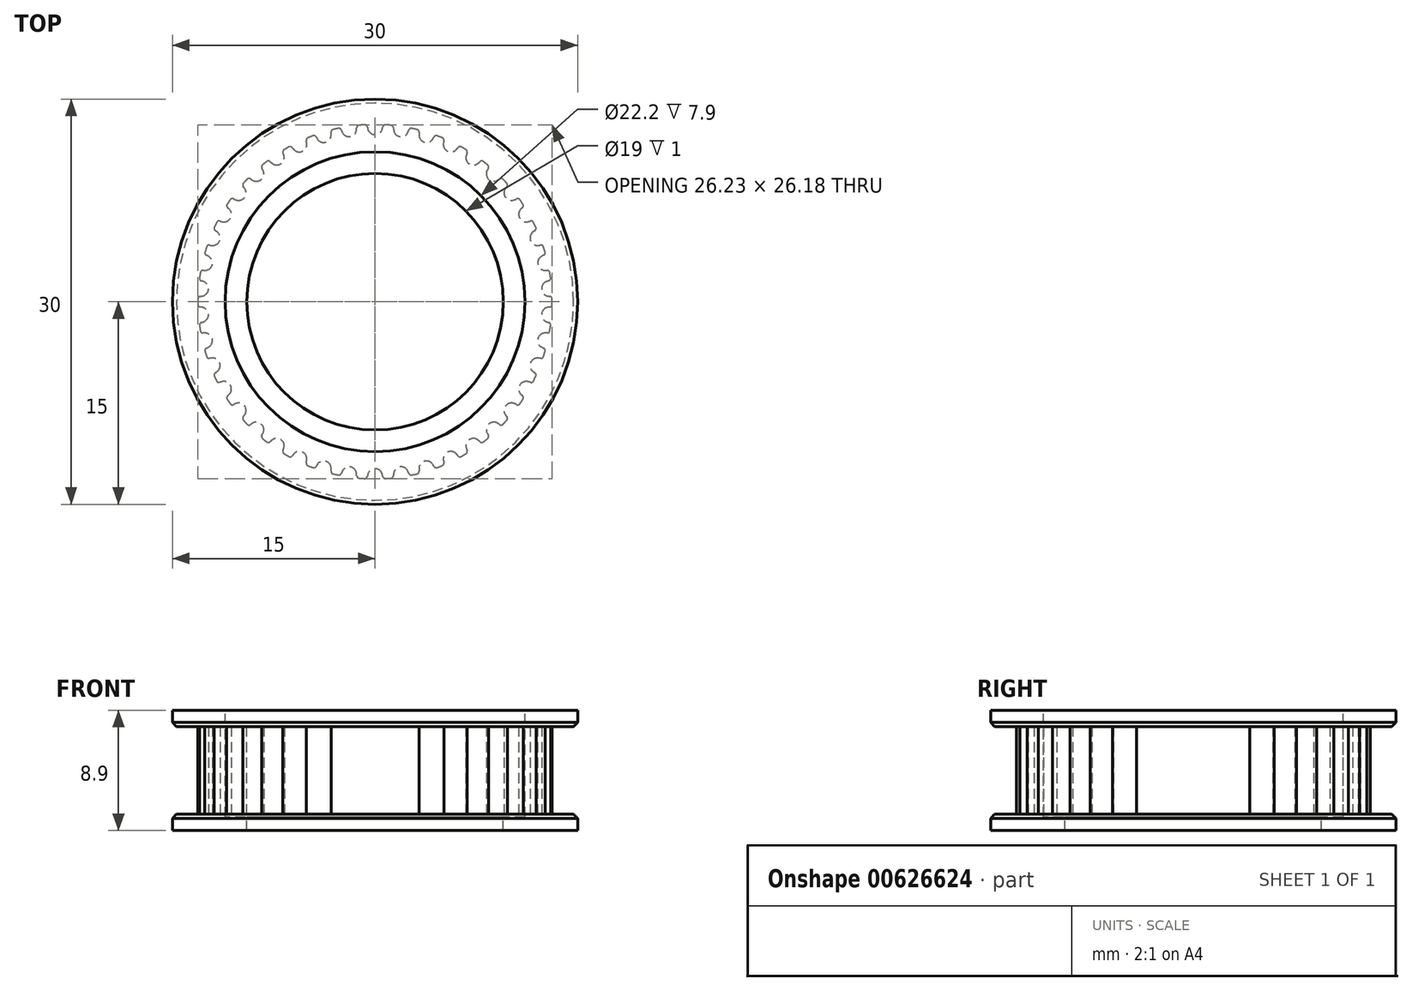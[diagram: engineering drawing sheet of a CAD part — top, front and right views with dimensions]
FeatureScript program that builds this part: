
annotation { "Feature Type Name" : "Feature", "Feature Type Description" : "" }
export const myFeature = defineFeature(function(context is Context, id is Id, definition is map)
    precondition{}
    {
        {
            assignVariable(context, id + "F0", {"name" : "teeth", "anyValue" : 42});
        }
        {
            assignVariable(context, id + "F1", {"name" : "belt_width", "anyValue" : 6.5});
        }
        {
            var Q0;
            Q0=qCreatedBy(makeId("Top.planeOp"),FACE);
            var sketch = newSketch(context, id + "F2", { "sketchPlane" : qUnion([Q0])});
            skLineSegment(sketch, "E0", {"start": v(0, 0) * mm, "end": v(0, 12.37) * mm, "construction": true});
            skCircle(sketch, "E1", {"center": v(0, 0) * mm, "radius": 13.12 * mm});
            skPoint(sketch, "E2.MirrorCS.end.orphan", {"position": v(0.98, 13.08) * mm});
            skLineSegment(sketch, "E3", {"start": v(0.98, 13.08) * mm, "end": v(1, 13.33) * mm, "construction": true});
            skLineSegment(sketch, "E4", {"start": v(-0.98, 13.08) * mm, "end": v(-1, 13.33) * mm, "construction": true});
            skArc(sketch, "E5", {"start": v(0, 12.37) * mm, "mid": v(0.34, 12.48) * mm, "end": v(0.54, 12.77) * mm});
            skArc(sketch, "E6", {"start": v(0.54, 12.77) * mm, "mid": v(0.56, 12.87) * mm, "end": v(0.58, 12.97) * mm, "construction": true});
            skLineSegment(sketch, "E7", {"start": v(0, 12.37) * mm, "end": v(0, 13.12) * mm, "construction": true});
            skLineSegment(sketch, "E8", {"start": v(0, 13.12) * mm, "end": v(0, 13.37) * mm, "construction": true});
            skArc(sketch, "E9", {"start": v(0.58, 12.97) * mm, "mid": v(0.64, 13.06) * mm, "end": v(0.74, 13.1) * mm, "construction": true});
            skArc(sketch, "E10", {"start": v(1, 13.33) * mm, "mid": v(0, 13.37) * mm, "end": v(-1, 13.33) * mm, "construction": true});
            skLineSegment(sketch, "E11", {"start": v(0.98, 13.08) * mm, "end": v(0.92, 12.33) * mm});
            skLineSegment(sketch, "E12", {"start": v(0.92, 12.33) * mm, "end": v(0, 0) * mm});
            skLineSegment(sketch, "E13", {"start": v(0, 0) * mm, "end": v(-0.92, 12.33) * mm});
            skLineSegment(sketch, "E14", {"start": v(-0.92, 12.33) * mm, "end": v(-0.98, 13.08) * mm});
            skArc(sketch, "E15", {"start": v(0.77, 13.1) * mm, "mid": v(0.65, 13.06) * mm, "end": v(0.58, 12.95) * mm});
            skArc(sketch, "E16", {"start": v(0.54, 12.77) * mm, "mid": v(0.56, 12.86) * mm, "end": v(0.58, 12.95) * mm});
            skArc(sketch, "E17.MirrorCS", {"start": v(0, 12.37) * mm, "mid": v(-0.34, 12.48) * mm, "end": v(-0.54, 12.77) * mm});
            skArc(sketch, "E18.MirrorCS", {"start": v(-0.54, 12.77) * mm, "mid": v(-0.56, 12.86) * mm, "end": v(-0.58, 12.95) * mm});
            skArc(sketch, "E19.MirrorCS", {"start": v(-0.77, 13.1) * mm, "mid": v(-0.65, 13.06) * mm, "end": v(-0.58, 12.95) * mm});
            skArc(sketch, "E20", {"start": v(0, 13.12) * mm, "mid": v(-0.2, 13.11) * mm, "end": v(-0.4, 13.1) * mm});
            skArc(sketch, "E21", {"start": v(0.92, 12.33) * mm, "mid": v(0, 12.37) * mm, "end": v(-0.92, 12.33) * mm, "construction": true});
            skLineSegment(sketch, "E22", {"start": v(1, 13.33) * mm, "end": v(1.03, 13.7) * mm, "construction": true});
            skLineSegment(sketch, "E23", {"start": v(-1, 13.33) * mm, "end": v(-1.03, 13.7) * mm, "construction": true});
            skArc(sketch, "E24", {"start": v(-1.03, 13.7) * mm, "mid": v(0, 13.75) * mm, "end": v(1.03, 13.7) * mm, "construction": true});
            skSolve(sketch);
        }
        {
            var Q0;
            Q0=makeQuery(id+"F2.imprint","IMPRINT",FACE,{"disambiguationData":[TD([[makeQuery(id+"F2.imprint","IMPRINT",EDGE,{"derivedFrom":sQuery(id+"F2.wireOp",EDGE,"E5")}),-1.0]])]});
            var Q1;
            {var subQ1=sQuery(id+"F2.wireOp",EDGE,"E14");Q1=makeQuery(id+"F2.imprint","IMPRINT",FACE,{"disambiguationData":[TD([[makeQuery(id+"F2.imprint","IMPRINT",EDGE,{"derivedFrom":subQ1}),-1.0]])]});}
            var Q2;
            {var subQ0=sQuery(id+"F2.wireOp",EDGE,"E12");Q2=makeQuery(id+"F2.imprint","IMPRINT",FACE,{"disambiguationData":[TD([[makeQuery(id+"F2.imprint","IMPRINT",EDGE,{"derivedFrom":subQ0}),-1.0]])]});}
            extrude(context, id + "F3", {"entities" : qUnion([Q0, Q1, Q2]), "depth" : (getVariable(context, 'belt_width')) * mm, "symmetric" : true});
        }
        {
            var Q0;
            Q0=makeQuery(id+"F3.opExtrude","SWEPT_BODY",BODY,{"disambiguationData":[OSD([sQuery(id+"F2.wireOp",EDGE,"E1"),sQuery(id+"F2.wireOp",EDGE,"E5"),sQuery(id+"F2.wireOp",EDGE,"E11"),sQuery(id+"F2.wireOp",EDGE,"E12"),sQuery(id+"F2.wireOp",EDGE,"E13"),sQuery(id+"F2.wireOp",EDGE,"E14"),sQuery(id+"F2.wireOp",EDGE,"E15"),sQuery(id+"F2.wireOp",EDGE,"E16"),sQuery(id+"F2.wireOp",EDGE,"E17.MirrorCS"),sQuery(id+"F2.wireOp",EDGE,"E18.MirrorCS"),sQuery(id+"F2.wireOp",EDGE,"E19.MirrorCS")])]});
            var Q1;
            Q1=makeQuery(id+"F3.opExtrude","SWEPT_EDGE",EDGE,{"disambiguationData":[OSD([sQuery(id+"F2.wireOp",EDGE,"E12"),sQuery(id+"F2.wireOp",EDGE,"E13")])]});
            circularPattern(context, id + "F4", {"operationType" : NewBodyOperationType.ADD, "entities" : qUnion([Q0]), "axis" : qUnion([Q1]), "angle" : 360 * degree, "instanceCount" : getVariable(context, 'teeth'), "equalSpace" : true});
        }
        {
            var Q0;
            Q0=qCreatedBy(makeId("Front.planeOp"),FACE);
            var sketch = newSketch(context, id + "F5", { "sketchPlane" : qUnion([Q0])});
            skLineSegment(sketch, "E25", {"start": v(0, -3.25) * mm, "end": v(13.12, -3.25) * mm});
            skLineSegment(sketch, "E26", {"start": v(13.12, -3.25) * mm, "end": v(15, -3.25) * mm});
            skLineSegment(sketch, "E27", {"start": v(0, 3.25) * mm, "end": v(13.12, 3.25) * mm});
            skLineSegment(sketch, "E28", {"start": v(15, 3.25) * mm, "end": v(13.12, 3.25) * mm});
            skLineSegment(sketch, "E29", {"start": v(15, 3.25) * mm, "end": v(15, 4.45) * mm});
            skLineSegment(sketch, "E30", {"start": v(15, 4.45) * mm, "end": v(0, 4.45) * mm});
            skLineSegment(sketch, "E31", {"start": v(0, 4.45) * mm, "end": v(0, 3.25) * mm});
            skLineSegment(sketch, "E32", {"start": v(13.12, 0) * mm, "end": v(13.12, -3.25) * mm, "construction": true});
            skLineSegment(sketch, "E33", {"start": v(15, -4.45) * mm, "end": v(0, -4.45) * mm});
            skLineSegment(sketch, "E34", {"start": v(15, -3.25) * mm, "end": v(15, -4.45) * mm});
            skLineSegment(sketch, "E35", {"start": v(0, -3.25) * mm, "end": v(0, -4.45) * mm});
            skLineSegment(sketch, "E36", {"start": v(0, 4.45) * mm, "end": v(0, -4.45) * mm, "construction": true});
            skSolve(sketch);
        }
        {
            var Q0;
            Q0=makeQuery(id+"F5.imprint","IMPRINT",FACE,{"disambiguationData":[TD([[makeQuery(id+"F5.imprint","IMPRINT",EDGE,{"derivedFrom":sQuery(id+"F5.wireOp",EDGE,"E25")}),-1.0]])]});
            var Q1;
            Q1=makeQuery(id+"F5.imprint","IMPRINT",FACE,{"disambiguationData":[TD([[makeQuery(id+"F5.imprint","IMPRINT",EDGE,{"derivedFrom":sQuery(id+"F5.wireOp",EDGE,"E27")}),1.0]])]});
            var Q2;
            Q2=qConstructionFilter(qBodyType(qCreatedBy(id+"F5",EDGE),BodyType.WIRE),ConstructionObject.NO);
            var Q3;
            Q3=sQuery(id+"F5.wireOp",EDGE,"E36");
            revolve(context, id + "F6", {"operationType" : NewBodyOperationType.ADD, "entities" : qUnion([Q0, Q1]), "surfaceEntities" : qUnion([Q2]), "axis" : qUnion([Q3]), "revolveType" : RevolveType.FULL});
        }
        {
            var Q0;
            Q0=makeQuery(id+"F6.opRevolve","SWEPT_FACE",FACE,{"disambiguationData":[OSD([sQuery(id+"F5.wireOp",EDGE,"E30")])]});
            var sketch = newSketch(context, id + "F7", { "sketchPlane" : qUnion([Q0])});
            skPoint(sketch, "E37", {"position": v(0, 0) * mm});
            skCircle(sketch, "E38", {"center": v(0, 0) * mm, "radius": 11.1 * mm});
            skCircle(sketch, "E39", {"center": v(0, 0) * mm, "radius": 9.5 * mm});
            skSolve(sketch);
        }
        {
            var Q0;
            Q0=makeQuery(id+"F7.imprint","IMPRINT",FACE,{"disambiguationData":[TD([[makeQuery(id+"F7.imprint","IMPRINT",EDGE,{"derivedFrom":sQuery(id+"F7.wireOp",EDGE,"E38")}),1.0]])]});
            extrude(context, id + "F8", {"entities" : qUnion([Q0]), "operationType" : NewBodyOperationType.REMOVE, "oppositeDirection" : true, "depth" : 7.9 * mm});
        }
        {
            var Q0;
            Q0=makeQuery(id+"F8.boolean.opBoolean","SPLIT",FACE,{"disambiguationData":[TD([makeQuery(id+"F8.opExtrude","SWEPT_FACE",FACE,{"disambiguationData":[OSD([sQuery(id+"F7.wireOp",EDGE,"E39")])]})])],"derivedFrom":makeQuery(id+"F6.opRevolve","SWEPT_FACE",FACE,{"disambiguationData":[OSD([sQuery(id+"F5.wireOp",EDGE,"E30")])]})});
            extrude(context, id + "F9", {"entities" : qUnion([Q0]), "operationType" : NewBodyOperationType.REMOVE, "endBound" : BoundingType.UP_TO_NEXT, "oppositeDirection" : true, "depth" : 25 * mm});
        }
        {
            var Q0;
            Q0=makeQuery(id+"F6.opRevolve","SWEPT_EDGE",EDGE,{"disambiguationData":[OSD([sQuery(id+"F5.wireOp",EDGE,"E26"),sQuery(id+"F5.wireOp",EDGE,"E34")])]});
            var Q1;
            Q1=makeQuery(id+"F6.opRevolve","SWEPT_EDGE",EDGE,{"disambiguationData":[OSD([sQuery(id+"F5.wireOp",EDGE,"E28"),sQuery(id+"F5.wireOp",EDGE,"E29")])]});
            chamfer(context, id + "F10", {"entities" : qUnion([Q0, Q1]), "width" : .3 * mm, "tangentPropagation" : true});
        }
    });
